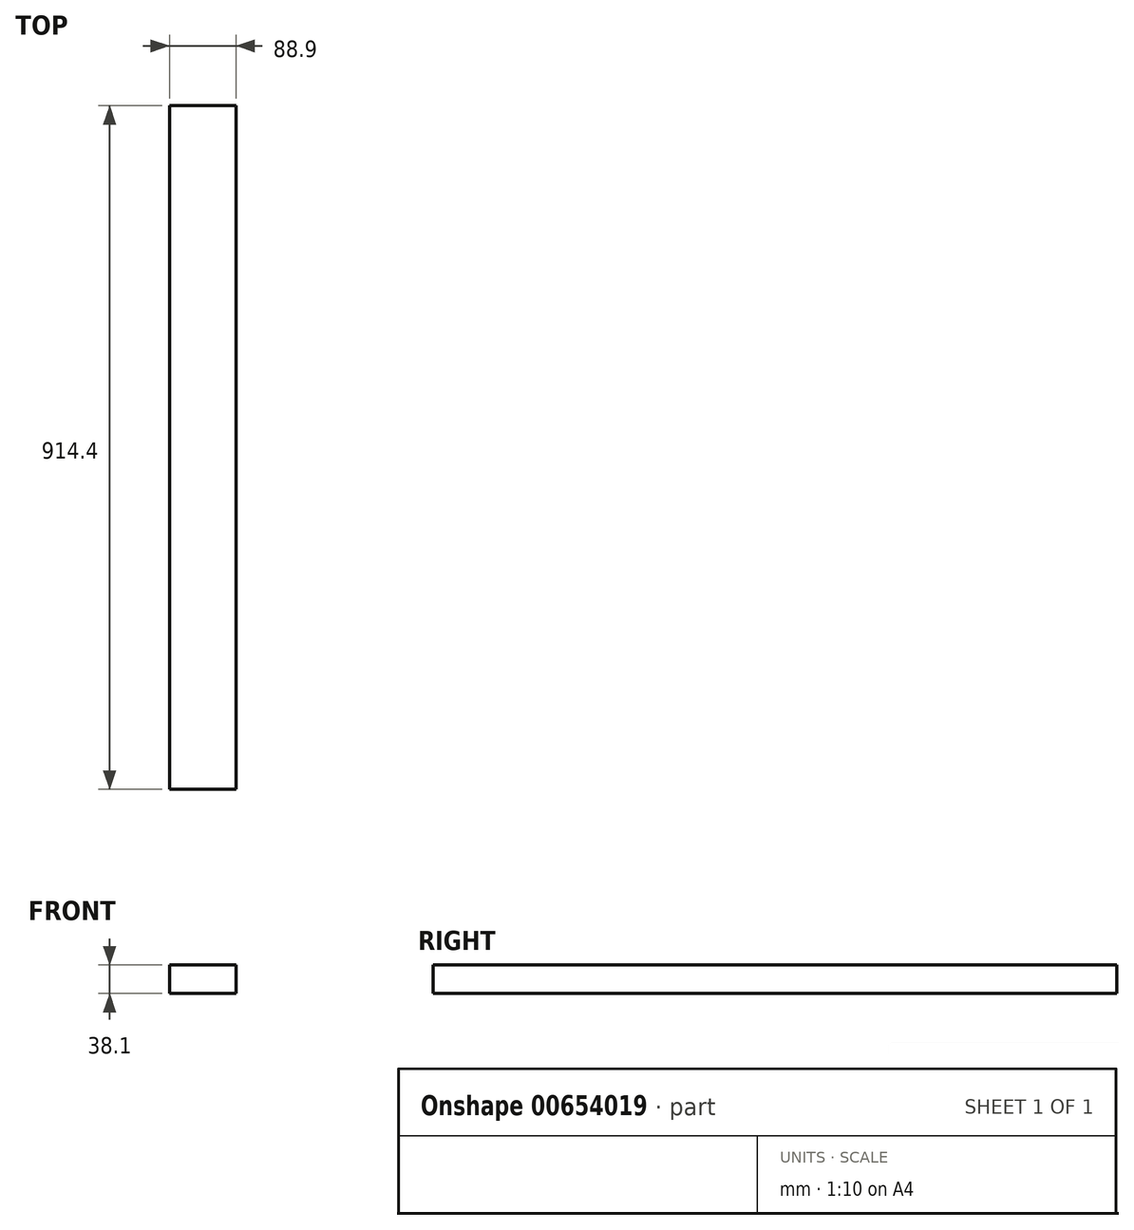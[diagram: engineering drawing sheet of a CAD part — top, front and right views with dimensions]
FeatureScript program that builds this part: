
annotation { "Feature Type Name" : "Feature", "Feature Type Description" : "" }
export const myFeature = defineFeature(function(context is Context, id is Id, definition is map)
    precondition{}
    {
        {
            var Q0;
            Q0=qCreatedBy(makeId("Front.planeOp"),FACE);
            var sketch = newSketch(context, id + "F0", { "sketchPlane" : qUnion([Q0])});
            skLineSegment(sketch, "E0.bottom", {"start": v(0, 0) * mm, "end": v(88.9, 0) * mm});
            skLineSegment(sketch, "E0.top", {"start": v(0, 38.1) * mm, "end": v(88.9, 38.1) * mm});
            skLineSegment(sketch, "E0.left", {"start": v(0, 0) * mm, "end": v(0, 38.1) * mm});
            skLineSegment(sketch, "E0.right", {"start": v(88.9, 0) * mm, "end": v(88.9, 38.1) * mm});
            skSolve(sketch);
        }
        {
            var Q0;
            Q0=makeQuery(id+"F0.imprint","IMPRINT",FACE,{"disambiguationData":[TD([[makeQuery(id+"F0.imprint","IMPRINT",EDGE,{"derivedFrom":sQuery(id+"F0.wireOp",EDGE,"E0.bottom")}),1.0]])]});
            extrude(context, id + "F1", {"entities" : qUnion([Q0]), "depth" : 914.4 * mm, "offsetDistance" : 25.4 * mm});
        }
    });
